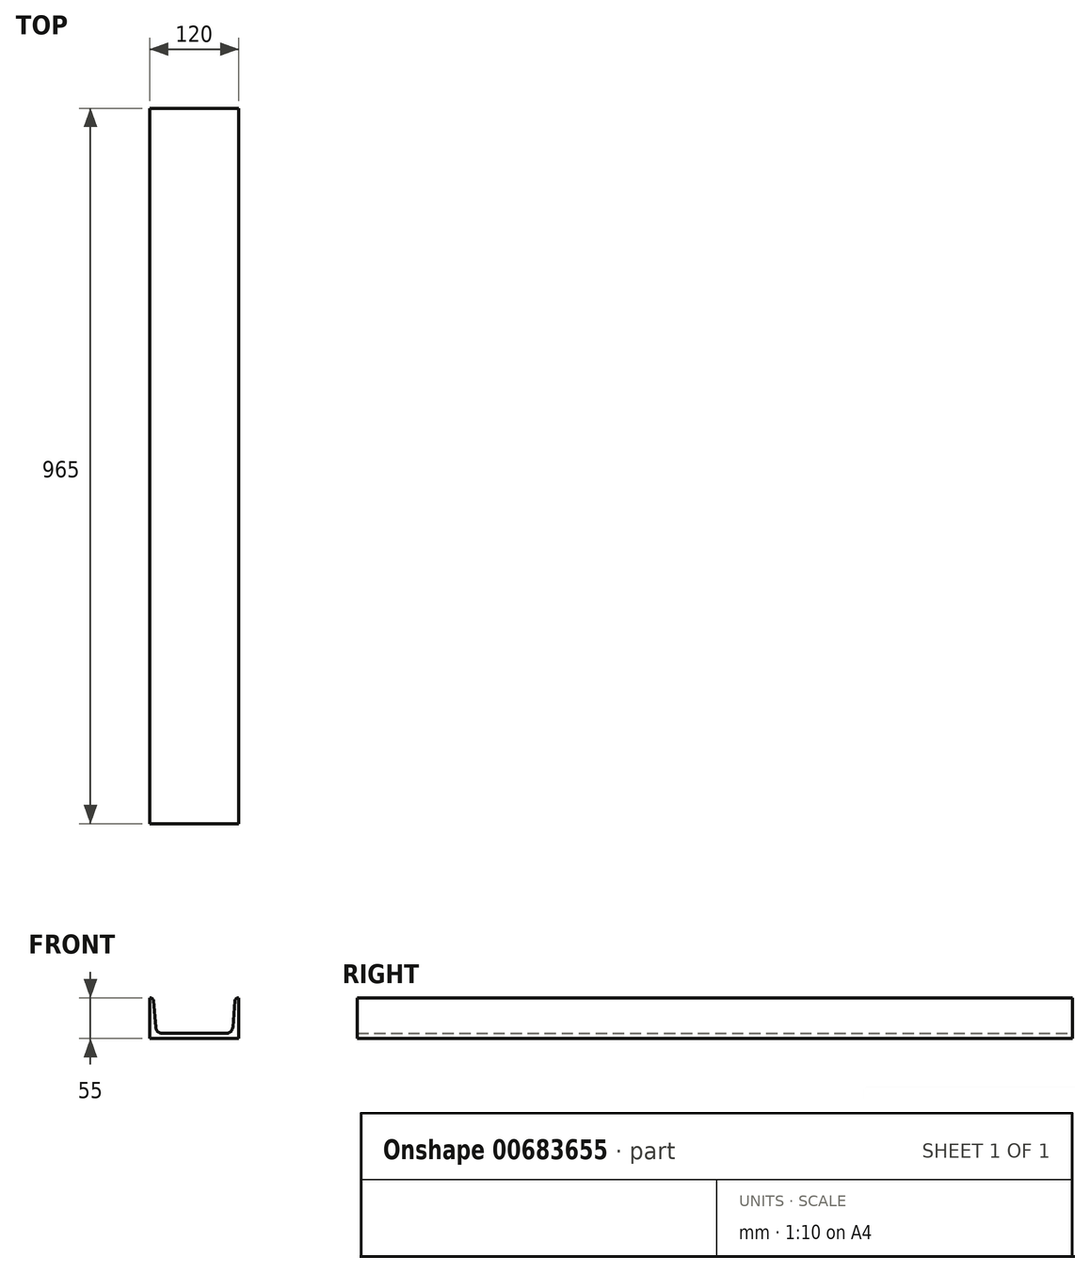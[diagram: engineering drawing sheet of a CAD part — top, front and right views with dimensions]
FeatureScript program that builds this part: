
annotation { "Feature Type Name" : "Feature", "Feature Type Description" : "" }
export const myFeature = defineFeature(function(context is Context, id is Id, definition is map)
    precondition{}
    {
        {
            var Q0;
            Q0=qCreatedBy(makeId("Front.planeOp"),FACE);
            var sketch = newSketch(context, id + "F0", { "sketchPlane" : qUnion([Q0])});
            skLineSegment(sketch, "E0", {"start": v(0, 55) * mm, "end": v(0, 0) * mm});
            skLineSegment(sketch, "E1", {"start": v(0, 0) * mm, "end": v(120, 0) * mm});
            skLineSegment(sketch, "E2", {"start": v(120, 0) * mm, "end": v(120, 55) * mm});
            skLineSegment(sketch, "E3.0", {"start": v(16.95, 7) * mm, "end": v(103.05, 7) * mm});
            skLineSegment(sketch, "E4", {"start": v(7.98, 15.28) * mm, "end": v(5.13, 50.86) * mm});
            skLineSegment(sketch, "E5", {"start": v(0, 55) * mm, "end": v(0.65, 55) * mm});
            skArc(sketch, "E6.filletArc", {"start": v(7.98, 15.28) * mm, "mid": v(10.84, 9.39) * mm, "end": v(16.95, 7) * mm});
            skPoint(sketch, "E7.visualSharp", {"position": v(4.8, 55) * mm});
            skArc(sketch, "E7.filletArc", {"start": v(5.13, 50.86) * mm, "mid": v(3.7, 53.8) * mm, "end": v(0.65, 55) * mm});
            skLineSegment(sketch, "E8", {"start": v(60, 0) * mm, "end": v(60, 20.87) * mm, "construction": true});
            skArc(sketch, "E9.MirrorCS", {"start": v(112.02, 15.28) * mm, "mid": v(109.16, 9.39) * mm, "end": v(103.05, 7) * mm});
            skLineSegment(sketch, "E10.MirrorCS", {"start": v(112.02, 15.28) * mm, "end": v(114.87, 50.86) * mm});
            skArc(sketch, "E11.MirrorCS", {"start": v(114.87, 50.86) * mm, "mid": v(116.3, 53.8) * mm, "end": v(119.35, 55) * mm});
            skLineSegment(sketch, "E12.MirrorCS", {"start": v(120, 55) * mm, "end": v(119.35, 55) * mm});
            skSolve(sketch);
        }
        {
            var Q0;
            Q0=makeQuery(id+"F0.imprint","IMPRINT",FACE,{"disambiguationData":[TD([[makeQuery(id+"F0.imprint","IMPRINT",EDGE,{"derivedFrom":sQuery(id+"F0.wireOp",EDGE,"E0")}),1.0]])]});
            extrude(context, id + "F1", {"entities" : qUnion([Q0]), "depth" : 965 * mm, "offsetDistance" : 25 * mm});
        }
    });
